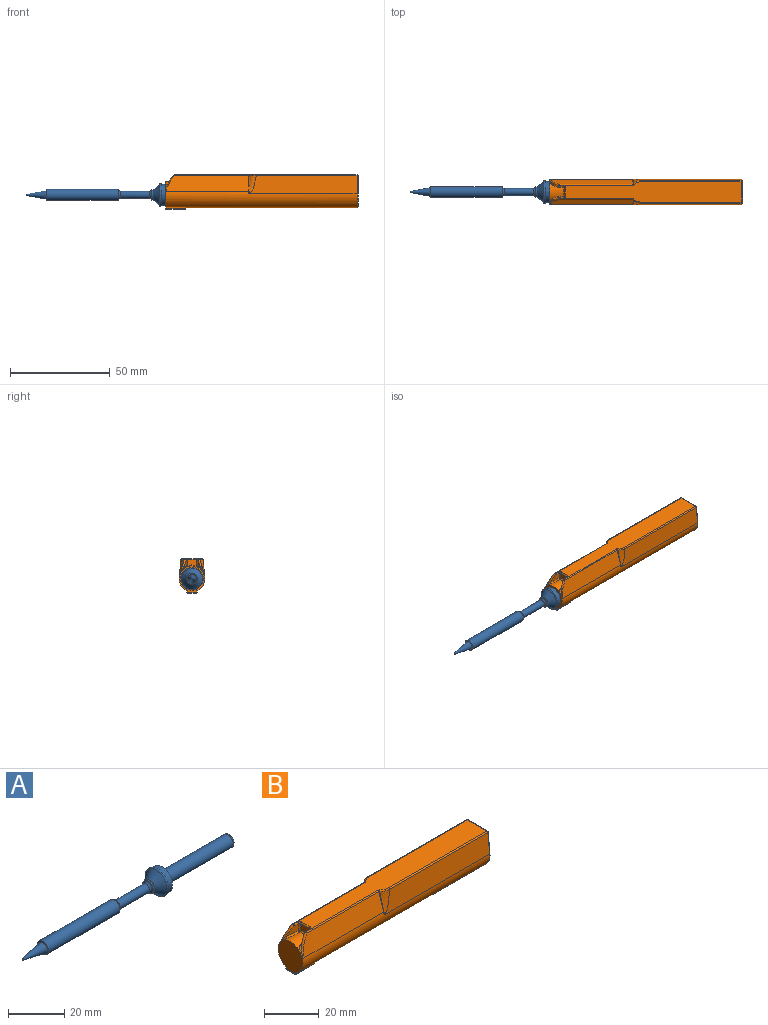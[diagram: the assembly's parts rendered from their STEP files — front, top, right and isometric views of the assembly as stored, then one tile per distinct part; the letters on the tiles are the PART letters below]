
ASSEMBLY  parts=2 mates=1
PART A: 15 faces, bbox 104.1x12.3x12.3 mm
  f0: plane 3.4x3.4mm, normal (1,0,0), area 9.1mm2, adj f12
  f1: cylinder r=2.7mm len=33mm, axis (1,0,0), area 559.8mm2, adj f2,f12
  f2: plane 10.6x10.6mm, normal (1,0,0), area 65.3mm2, adj f1,f3
  f3: cylinder r=5.3mm len=10.6mm, axis (1,0,0), area 74.9mm2, adj f2,f4
  f4: torus R=5.3mm, axis (1,0,0), area 43.9mm2, adj f3,f5
  f5: cone r=5.3mm half-angle=39.5deg, axis (1,0,0), area 104.8mm2, adj f4,f6
  f6: cylinder r=2.62mm len=5.25mm, axis (1,0,0), area 12.4mm2, adj f5,f13
  f7: cylinder r=1.8mm len=14.77mm, axis (1,0,0), area 167mm2, adj f13,f14
  f8: cylinder r=2.75mm len=36mm, axis (1,0,0), area 622mm2, adj f9,f14
  f9: plane 5.5x5.5mm, normal (-1,0,0), area 8.6mm2, adj f8,f10
  f10: cone r=2.2mm half-angle=10.3deg, axis (1,0,0), area 82.2mm2, adj f9,f11
  f11: sphere r=0.38mm, area 0.7mm2, adj f10
  f12: torus R=1.7mm, axis (-1,0,0), area 23.1mm2, adj f0,f1
  f13: torus R=2.8mm, axis (1,0,0), area 18.4mm2, adj f6,f7
  f14: torus R=2.8mm, axis (-1,0,0), area 20.5mm2, adj f7,f8
PART B: 69 faces, bbox 98.5x14.5x21 mm
  f0: cylinder r=6.45mm len=96mm, axis (-1,0,0), area 2152.6mm2, adj f2,f4,f5,f6,f7,f8,f9,f11
  f1: plane 15.6x11.9mm, normal (1,0,0), area 162mm2, adj f46,f50,f52,f53
  f2: plane 13.25x12.9mm, normal (-1,0,0), area 132.7mm2, adj f0,f58,f64,f65
  f3: plane 9x4.25mm, normal (0,0,-1), area 38.2mm2, adj f59,f62,f65,f68
  f4: plane 9x0.91mm, normal (0,1,0), area 8.2mm2, adj f0,f63,f64,f68
  f5: plane 9x0.91mm, normal (0,-1,0), area 8.2mm2, adj f0,f57,f58,f59
  f6: plane 4.25x0.71mm, normal (1,0,0), area 2mm2, adj f0,f57,f62,f63
  f7: plane 41.55x7.98mm, normal (0,0.96,0.28), area 329.6mm2, adj f0,f20,f36,f37
  f8: plane 54.79x9.64mm, normal (0,-1,0.1), area 471.5mm2, adj f0,f14,f15,f53,f56
  f9: plane 54.25x9.1mm, normal (0,1,0.1), area 471.5mm2, adj f0,f12,f13,f45,f46
  f10: plane 91.14x10.09mm, normal (0,0,1), area 772.9mm2, adj f28,f31,f35,f36,f38,f39,f41,f42
  f11: plane 41.55x7.98mm, normal (0,-0.96,0.28), area 329.6mm2, adj f0,f19,f47,f48
  f12: bspline ~11.52x4.08mm, area 23.8mm2, adj f9,f13,f33,f37,f42
  f13: bspline ~1.61x0.7mm, area 0.2mm2, adj f9,f12,f29
  f14: bspline ~11.52x4.08mm, area 23.8mm2, adj f8,f15,f43,f47,f54
  f15: bspline ~1.61x0.7mm, area 0.2mm2, adj f8,f14,f40
  f16: plane 4.44x3.06mm, normal (-1,0,0), area 12.5mm2, adj f26,f27,f34,f35
  f17: cylinder r=10mm len=5.24mm, axis (0,0,1), area 12.3mm2, adj f19,f25,f34,f41
  f18: cylinder r=10mm len=5.24mm, axis (0,0,1), area 12.3mm2, adj f20,f22,f27,f28
  f19: bspline ~13.5x7.26mm, area 9.7mm2, adj f11,f17,f23,f44
  f20: bspline ~13.5x7.26mm, area 9.7mm2, adj f7,f18,f21,f32
  f21: bspline ~4.26x2.97mm, area 1.6mm2, adj f0,f20,f22
  f22: bspline ~5.95x2.06mm, area 5.4mm2, adj f0,f18,f21,f24
  f23: bspline ~4.26x2.97mm, area 1.6mm2, adj f0,f19,f25
  f24: sphere r=0.5mm, area 0.4mm2, adj f22,f26,f27
  f25: bspline ~5.95x2.06mm, area 5.4mm2, adj f0,f17,f23,f30
  f26: torus R=6.95mm, axis (-1,0,0), area 3.4mm2, adj f0,f16,f24,f30
  f27: cylinder r=0.5mm len=3.06mm, axis (0,0,1), area 2.5mm2, adj f16,f18,f24,f31
  f28: torus R=9.5mm, axis (0,0,-1), area 1.6mm2, adj f10,f18,f31,f32
  f29: bspline ~1.32x0.27mm, area 0mm2, adj f0,f13,f33
  f30: sphere r=0.5mm, area 0.5mm2, adj f25,f26,f34
  f31: torus R=1mm, axis (0,0,-1), area 0.9mm2, adj f10,f27,f28,f35
  f32: sphere r=0.5mm, area 0.3mm2, adj f20,f28,f36
  f33: bspline ~0.12x0.06mm, area 0mm2, adj f0,f12,f29,f37
  f34: cylinder r=0.5mm len=3.06mm, axis (0,0,1), area 2.5mm2, adj f16,f17,f30,f38
  f35: cylinder r=0.5mm len=4.44mm, axis (0,1,0), area 3.5mm2, adj f10,f16,f31,f38
  f36: cylinder r=0.5mm len=36.68mm, axis (-1,0,0), area 23.6mm2, adj f7,f10,f32,f39
  f37: bspline ~9.12x2.65mm, area 2.2mm2, adj f7,f12,f33,f39
  f38: torus R=1mm, axis (0,0,-1), area 0.9mm2, adj f10,f34,f35,f41
  f39: bspline ~1x0.74mm, area 0.4mm2, adj f10,f36,f37,f42
  f40: bspline ~1.2x0.23mm, area 0mm2, adj f0,f15,f43
  f41: torus R=9.5mm, axis (0,0,-1), area 1.6mm2, adj f10,f17,f38,f44
  f42: bspline ~4.69x2.2mm, area 2.7mm2, adj f10,f12,f39,f45
  f43: bspline ~0.13x0.06mm, area 0mm2, adj f0,f14,f40,f47
  f44: sphere r=0.5mm, area 0.1mm2, adj f19,f41,f48
  f45: cylinder r=0.5mm len=50.51mm, axis (-1,0,0), area 37.2mm2, adj f9,f10,f42,f49
  f46: cylinder r=0.5mm len=9.13mm, axis (0,-0.1,1), area 7.2mm2, adj f1,f9,f49,f50
  f47: bspline ~9.12x2.65mm, area 2.2mm2, adj f11,f14,f43,f51
  f48: cylinder r=0.5mm len=36.68mm, axis (1,0,0), area 23.6mm2, adj f10,f11,f44,f51
  f49: sphere r=0.5mm, area 0.2mm2, adj f45,f46,f52
  f50: torus R=5.95mm, axis (1,0,0), area 16.4mm2, adj f0,f1,f46,f53
  f51: bspline ~0.93x0.68mm, area 0.4mm2, adj f10,f47,f48,f54
  f52: cylinder r=0.5mm len=10.09mm, axis (0,-1,0), area 7.9mm2, adj f1,f10,f49,f55
  f53: cylinder r=0.5mm len=9.13mm, axis (0,-0.1,-1), area 7.2mm2, adj f1,f8,f50,f55
  f54: bspline ~4.69x2.21mm, area 2.7mm2, adj f10,f14,f51,f56
  f55: sphere r=0.5mm, area 0.4mm2, adj f52,f53,f56
  f56: cylinder r=0.5mm len=50.51mm, axis (1,0,0), area 37.2mm2, adj f8,f10,f54,f55
  f57: cylinder r=0.5mm len=0.91mm, axis (0,0,1), area 0.6mm2, adj f0,f5,f6,f60
  f58: cylinder r=0.5mm len=0.91mm, axis (0,0,-1), area 0.6mm2, adj f0,f2,f5,f61
  f59: cylinder r=0.5mm len=9mm, axis (1,0,0), area 7.1mm2, adj f3,f5,f60,f61
  f60: sphere r=0.5mm, area 0.4mm2, adj f57,f59,f62
  f61: sphere r=0.5mm, area 0.4mm2, adj f58,f59,f65
  f62: cylinder r=0.5mm len=4.25mm, axis (0,-1,0), area 3.3mm2, adj f3,f6,f60,f66
  f63: cylinder r=0.5mm len=0.91mm, axis (0,0,-1), area 0.6mm2, adj f0,f4,f6,f66
  f64: cylinder r=0.5mm len=0.91mm, axis (0,0,1), area 0.6mm2, adj f0,f2,f4,f67
  f65: cylinder r=0.5mm len=4.25mm, axis (0,1,0), area 3.3mm2, adj f2,f3,f61,f67
  f66: sphere r=0.5mm, area 0.2mm2, adj f62,f63,f68
  f67: sphere r=0.5mm, area 0.5mm2, adj f64,f65,f68
  f68: cylinder r=0.5mm len=9mm, axis (-1,0,0), area 7.1mm2, adj f3,f4,f66,f67
PLACE A t=(0,8.86,0.93)mm
PLACE B t=(0,8.86,0.93)mm
MATE fastened B.f0 <-> A.f5  axis (-1,0,0) through (0,8.86,0.93)mm
